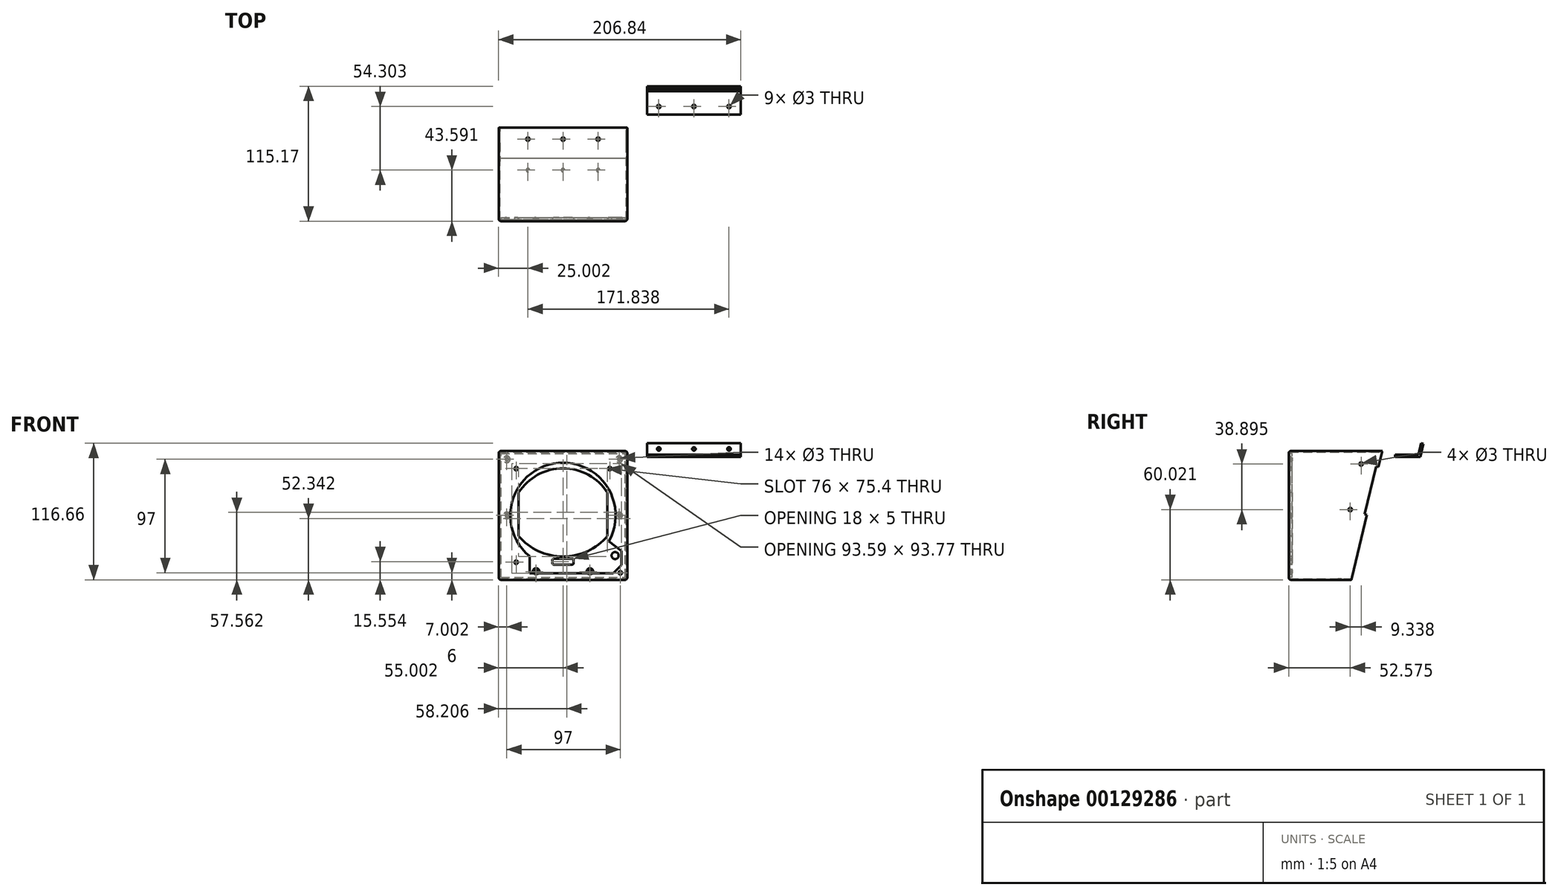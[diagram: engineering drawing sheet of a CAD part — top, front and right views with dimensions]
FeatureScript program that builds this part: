
annotation { "Feature Type Name" : "Feature", "Feature Type Description" : "" }
export const myFeature = defineFeature(function(context is Context, id is Id, definition is map)
    precondition{}
    {
        {
            var Q0;
            Q0=qCreatedBy(makeId("Front.planeOp"),FACE);
            var sketch = newSketch(context, id + "F0", { "sketchPlane" : qUnion([Q0])});
            skLineSegment(sketch, "E0.bottom", {"start": v(-56.84, -55) * mm, "end": v(-166.84, -55) * mm});
            skLineSegment(sketch, "E0.top", {"start": v(-56.84, 55) * mm, "end": v(-166.84, 55) * mm});
            skLineSegment(sketch, "E0.left", {"start": v(-56.84, -55) * mm, "end": v(-56.84, 55) * mm});
            skLineSegment(sketch, "E0.right", {"start": v(-166.84, -55) * mm, "end": v(-166.84, 55) * mm});
            skPoint(sketch, "E0.middle", {"position": v(-111.84, 0) * mm});
            skSolve(sketch);
        }
        {
            var Q0;
            Q0=makeQuery(id+"F0.imprint","IMPRINT",FACE,{"disambiguationData":[TD([[makeQuery(id+"F0.imprint","IMPRINT",EDGE,{"derivedFrom":sQuery(id+"F0.wireOp",EDGE,"E0.bottom")}),-1.0]])]});
            extrude(context, id + "F1", {"entities" : qUnion([Q0]), "endBound" : BoundingType.SYMMETRIC, "depth" : 120 * mm});
        }
        {
            var Q0;
            Q0=makeQuery(id+"F1.opExtrude","CAP_FACE",FACE,{"disambiguationData":[OSD([sQuery(id+"F0.wireOp",EDGE,"E0.bottom"),sQuery(id+"F0.wireOp",EDGE,"E0.top"),sQuery(id+"F0.wireOp",EDGE,"E0.left"),sQuery(id+"F0.wireOp",EDGE,"E0.right")])],"isStart":true});
            shell(context, id + "F2", {"entities" : qUnion([Q0]), "thickness" : 1 * mm});
        }
        {
            var Q0;
            Q0=makeQuery(id+"F1.opExtrude","SWEPT_FACE",FACE,{"disambiguationData":[OSD([sQuery(id+"F0.wireOp",EDGE,"E0.right")])]});
            var sketch = newSketch(context, id + "F3", { "sketchPlane" : qUnion([Q0])});
            skLineSegment(sketch, "E1", {"start": v(-20, 55) * mm, "end": v(6.4, -55) * mm});
            skLineSegment(sketch, "E2", {"start": v(6.4, -55) * mm, "end": v(-89.83, -55) * mm});
            skLineSegment(sketch, "E3", {"start": v(-89.83, -55) * mm, "end": v(-89.83, 55) * mm});
            skLineSegment(sketch, "E4", {"start": v(-89.83, 55) * mm, "end": v(-20, 55) * mm});
            skCircle(sketch, "E5", {"center": v(-1.91, 43.92) * mm, "radius": 1.5 * mm});
            skCircle(sketch, "E6", {"center": v(7.43, 5.02) * mm, "radius": 1.5 * mm});
            skLineSegment(sketch, "E7", {"start": v(-11.83, 20.97) * mm, "end": v(26.98, 30.28) * mm, "construction": true});
            skLineSegment(sketch, "E8", {"start": v(-16.73, 41.39) * mm, "end": v(-6.93, 0.55) * mm});
            skLineSegment(sketch, "E9", {"start": v(-6.93, 0.55) * mm, "end": v(-4.98, 1.01) * mm});
            skLineSegment(sketch, "E10", {"start": v(-4.98, 1.01) * mm, "end": v(-14.79, 41.85) * mm});
            skLineSegment(sketch, "E11", {"start": v(-14.79, 41.85) * mm, "end": v(-16.73, 41.39) * mm});
            skSolve(sketch);
        }
        {
            var Q0;
            Q0=qSketchRegion(id+"F3",true);
            extrude(context, id + "F4", {"entities" : qUnion([Q0]), "operationType" : NewBodyOperationType.REMOVE, "oppositeDirection" : true, "depth" : 110 * mm});
        }
        {
            var Q0;
            Q0=makeQuery(id+"F1.opExtrude","CAP_EDGE",EDGE,{"disambiguationData":[OSD([sQuery(id+"F0.wireOp",EDGE,"E0.right")])],"isStart":false});
            var Q1;
            Q1=makeQuery(id+"F1.opExtrude","SWEPT_EDGE",EDGE,{"disambiguationData":[OSD([sQuery(id+"F0.wireOp",EDGE,"E0.top"),sQuery(id+"F0.wireOp",EDGE,"E0.right")])]});
            var Q2;
            Q2=makeQuery(id+"F1.opExtrude","CAP_EDGE",EDGE,{"disambiguationData":[OSD([sQuery(id+"F0.wireOp",EDGE,"E0.top")])],"isStart":false});
            var Q3;
            Q3=makeQuery(id+"F1.opExtrude","CAP_EDGE",EDGE,{"disambiguationData":[OSD([sQuery(id+"F0.wireOp",EDGE,"E0.left")])],"isStart":false});
            var Q4;
            Q4=makeQuery(id+"F1.opExtrude","SWEPT_EDGE",EDGE,{"disambiguationData":[OSD([sQuery(id+"F0.wireOp",EDGE,"E0.top"),sQuery(id+"F0.wireOp",EDGE,"E0.left")])]});
            var Q5;
            Q5=makeQuery(id+"F1.opExtrude","CAP_EDGE",EDGE,{"disambiguationData":[OSD([sQuery(id+"F0.wireOp",EDGE,"E0.bottom")])],"isStart":false});
            var Q6;
            Q6=makeQuery(id+"F1.opExtrude","SWEPT_EDGE",EDGE,{"disambiguationData":[OSD([sQuery(id+"F0.wireOp",EDGE,"E0.bottom"),sQuery(id+"F0.wireOp",EDGE,"E0.left")])]});
            var Q7;
            Q7=makeQuery(id+"F1.opExtrude","SWEPT_EDGE",EDGE,{"disambiguationData":[OSD([sQuery(id+"F0.wireOp",EDGE,"E0.bottom"),sQuery(id+"F0.wireOp",EDGE,"E0.right")])]});
            fillet(context, id + "F5", {"entities" : qUnion([Q0, Q1, Q2, Q3, Q4, Q5, Q6, Q7]), "radius" : 2 * mm, "tangentPropagation" : true, "allowEdgeOverflow" : false});
        }
        {
            var Q0;
            Q0=makeQuery(id+"F1.opExtrude","CAP_FACE",FACE,{"disambiguationData":[OSD([sQuery(id+"F0.wireOp",EDGE,"E0.bottom"),sQuery(id+"F0.wireOp",EDGE,"E0.top"),sQuery(id+"F0.wireOp",EDGE,"E0.left"),sQuery(id+"F0.wireOp",EDGE,"E0.right")])],"isStart":false});
            var sketch = newSketch(context, id + "F6", { "sketchPlane" : qUnion([Q0])});
            skCircle(sketch, "E12", {"center": v(-111.84, 0) * mm, "radius": 45 * mm});
            skLineSegment(sketch, "E13", {"start": v(-140.4, -34.77) * mm, "end": v(-140.4, -49.54) * mm});
            skLineSegment(sketch, "E14", {"start": v(-140.4, -49.54) * mm, "end": v(-68.8, -49.54) * mm});
            skLineSegment(sketch, "E15", {"start": v(-68.8, -49.54) * mm, "end": v(-61.84, -42.48) * mm});
            skLineSegment(sketch, "E16", {"start": v(-61.84, -42.48) * mm, "end": v(-61.84, -30.48) * mm});
            skLineSegment(sketch, "E17", {"start": v(-61.84, -30.48) * mm, "end": v(-72.6, -22.03) * mm});
            skCircle(sketch, "E18", {"center": v(-151.84, 40) * mm, "radius": 1.5 * mm});
            skCircle(sketch, "E19", {"center": v(-71.84, 40) * mm, "radius": 1.5 * mm});
            skCircle(sketch, "E20", {"center": v(-151.84, -40) * mm, "radius": 1.5 * mm});
            skCircle(sketch, "E21", {"center": v(-62.84, -49) * mm, "radius": 1.5 * mm});
            skSolve(sketch);
        }
        {
            var Q0;
            Q0=qSketchRegion(id+"F6",true);
            extrude(context, id + "F7", {"entities" : qUnion([Q0]), "operationType" : NewBodyOperationType.REMOVE, "oppositeDirection" : true, "depth" : 1 * mm});
        }
        {
            var Q0;
            Q0=makeQuery(id+"F2.opShell","OFFSET_FACE",FACE,{"disambiguationData":[OSD([sQuery(id+"F0.wireOp",EDGE,"E0.bottom"),sQuery(id+"F0.wireOp",EDGE,"E0.top"),sQuery(id+"F0.wireOp",EDGE,"E0.left"),sQuery(id+"F0.wireOp",EDGE,"E0.right")])]});
            var sketch = newSketch(context, id + "F8", { "sketchPlane" : qUnion([Q0])});
            skLineSegment(sketch, "E22.bottom", {"start": v(164.84, -53) * mm, "end": v(58.84, -53) * mm});
            skLineSegment(sketch, "E22.top", {"start": v(164.84, 53) * mm, "end": v(58.84, 53) * mm});
            skLineSegment(sketch, "E22.left", {"start": v(164.84, -53) * mm, "end": v(164.84, 53) * mm});
            skLineSegment(sketch, "E22.right", {"start": v(58.84, -53) * mm, "end": v(58.84, 53) * mm});
            skPoint(sketch, "E22.middle", {"position": v(111.84, 0) * mm});
            skLineSegment(sketch, "E23", {"start": v(73.84, 19.37) * mm, "end": v(73.84, -17.63) * mm});
            skLineSegment(sketch, "E24", {"start": v(149.84, 19.37) * mm, "end": v(149.84, -17.63) * mm});
            skArc(sketch, "E25", {"start": v(149.84, 19.37) * mm, "mid": v(111.84, 40.26) * mm, "end": v(73.84, 19.37) * mm});
            skArc(sketch, "E26", {"start": v(73.84, -17.63) * mm, "mid": v(111.84, -35.14) * mm, "end": v(149.84, -17.63) * mm});
            skLineSegment(sketch, "E27.bottom", {"start": v(103.84, -36.95) * mm, "end": v(119.84, -36.95) * mm});
            skLineSegment(sketch, "E27.top", {"start": v(103.84, -41.95) * mm, "end": v(119.84, -41.95) * mm});
            skLineSegment(sketch, "E27.left", {"start": v(102.84, -37.95) * mm, "end": v(102.84, -40.95) * mm});
            skLineSegment(sketch, "E27.right", {"start": v(120.84, -37.95) * mm, "end": v(120.84, -40.95) * mm});
            skPoint(sketch, "E28.visualSharp", {"position": v(102.84, -36.95) * mm});
            skArc(sketch, "E28.filletArc", {"start": v(103.84, -36.95) * mm, "mid": v(103.13, -37.24) * mm, "end": v(102.84, -37.95) * mm});
            skPoint(sketch, "E29.visualSharp", {"position": v(102.84, -41.95) * mm});
            skArc(sketch, "E29.filletArc", {"start": v(102.84, -40.95) * mm, "mid": v(103.13, -41.65) * mm, "end": v(103.84, -41.95) * mm});
            skPoint(sketch, "E30.visualSharp", {"position": v(120.84, -36.95) * mm});
            skArc(sketch, "E30.filletArc", {"start": v(120.84, -37.95) * mm, "mid": v(120.55, -37.24) * mm, "end": v(119.84, -36.95) * mm});
            skPoint(sketch, "E31.visualSharp", {"position": v(120.84, -41.95) * mm});
            skArc(sketch, "E31.filletArc", {"start": v(119.84, -41.95) * mm, "mid": v(120.55, -41.65) * mm, "end": v(120.84, -40.95) * mm});
            skPoint(sketch, "E32", {"position": v(111.84, -39.45) * mm});
            skCircle(sketch, "E33", {"center": v(151.84, 40) * mm, "radius": 1.5 * mm});
            skCircle(sketch, "E34", {"center": v(71.84, 40) * mm, "radius": 1.5 * mm});
            skCircle(sketch, "E35", {"center": v(62.84, -49) * mm, "radius": 1.5 * mm});
            skCircle(sketch, "E36", {"center": v(151.84, -40) * mm, "radius": 1.5 * mm});
            skCircle(sketch, "E37", {"center": v(67.34, -34.27) * mm, "radius": 3 * mm});
            skSolve(sketch);
        }
        {
            var Q0;
            Q0=qSketchRegion(id+"F8",true);
            extrude(context, id + "F9", {"entities" : qUnion([Q0]), "depth" : 2 * mm});
        }
        {
            var Q0;
            Q0=makeQuery(id+"F9.opExtrude","CAP_FACE",FACE,{"disambiguationData":[OSD([sQuery(id+"F8.wireOp",EDGE,"E22.bottom"),sQuery(id+"F8.wireOp",EDGE,"E22.top"),sQuery(id+"F8.wireOp",EDGE,"E22.left"),sQuery(id+"F8.wireOp",EDGE,"E22.right"),sQuery(id+"F8.wireOp",EDGE,"E23"),sQuery(id+"F8.wireOp",EDGE,"E24"),sQuery(id+"F8.wireOp",EDGE,"E25"),sQuery(id+"F8.wireOp",EDGE,"E26"),sQuery(id+"F8.wireOp",EDGE,"E27.bottom"),sQuery(id+"F8.wireOp",EDGE,"E27.top"),sQuery(id+"F8.wireOp",EDGE,"E27.left"),sQuery(id+"F8.wireOp",EDGE,"E27.right"),sQuery(id+"F8.wireOp",EDGE,"E28.filletArc"),sQuery(id+"F8.wireOp",EDGE,"E29.filletArc"),sQuery(id+"F8.wireOp",EDGE,"E30.filletArc"),sQuery(id+"F8.wireOp",EDGE,"E31.filletArc"),sQuery(id+"F8.wireOp",EDGE,"E33"),sQuery(id+"F8.wireOp",EDGE,"E34"),sQuery(id+"F8.wireOp",EDGE,"E35"),sQuery(id+"F8.wireOp",EDGE,"E36"),sQuery(id+"F8.wireOp",EDGE,"E37")])],"isStart":true});
            var sketch = newSketch(context, id + "F10", { "sketchPlane" : qUnion([Q0])});
            skLineSegment(sketch, "E38.bottom", {"start": v(-72.84, -43) * mm, "end": v(-150.84, -43) * mm});
            skLineSegment(sketch, "E38.top", {"start": v(-72.84, 43) * mm, "end": v(-150.84, 43) * mm});
            skLineSegment(sketch, "E38.left", {"start": v(-72.84, -43) * mm, "end": v(-72.84, 43) * mm});
            skLineSegment(sketch, "E38.right", {"start": v(-150.84, -43) * mm, "end": v(-150.84, 43) * mm});
            skPoint(sketch, "E38.middle", {"position": v(-111.84, 0) * mm});
            skLineSegment(sketch, "E39.bottom", {"start": v(-56.84, -55) * mm, "end": v(-166.84, -55) * mm});
            skLineSegment(sketch, "E39.top", {"start": v(-56.84, 55) * mm, "end": v(-166.84, 55) * mm});
            skLineSegment(sketch, "E39.left", {"start": v(-56.84, -55) * mm, "end": v(-56.84, 55) * mm});
            skLineSegment(sketch, "E39.right", {"start": v(-166.84, -55) * mm, "end": v(-166.84, 55) * mm});
            skSolve(sketch);
        }
        {
            var Q0;
            {var subQ10=sQuery(id+"F10.wireOp",EDGE,"E38.bottom");Q0=makeQuery(id+"F10.imprint","IMPRINT",FACE,{"disambiguationData":[TD([[makeQuery(id+"F10.imprint","IMPRINT",EDGE,{"derivedFrom":subQ10}),1.0]])]});}
            var sketch = newSketch(context, id + "F11", { "sketchPlane" : qUnion([Q0])});
            skCircle(sketch, "E40", {"center": v(-159.84, 48) * mm, "radius": 1.5 * mm});
            skCircle(sketch, "E41", {"center": v(-63.84, 48) * mm, "radius": 1.5 * mm});
            skCircle(sketch, "E42", {"center": v(-88.84, -48) * mm, "radius": 1.5 * mm});
            skCircle(sketch, "E43", {"center": v(-134.84, -48) * mm, "radius": 1.5 * mm});
            skCircle(sketch, "E44", {"center": v(-159.84, 0) * mm, "radius": 1.5 * mm});
            skCircle(sketch, "E45", {"center": v(-63.84, 0) * mm, "radius": 1.5 * mm});
            skSolve(sketch);
        }
        {
            var Q0;
            Q0=sQuery(id+"F11.wireOp",VERTEX,"E43.center");
            var Q1;
            Q1=sQuery(id+"F11.wireOp",VERTEX,"E42.center");
            var Q2;
            Q2=sQuery(id+"F11.wireOp",VERTEX,"E40.center");
            var Q3;
            Q3=sQuery(id+"F11.wireOp",VERTEX,"E41.center");
            var Q4;
            Q4=sQuery(id+"F11.wireOp",VERTEX,"E44.center");
            var Q5;
            Q5=sQuery(id+"F11.wireOp",VERTEX,"E45.center");
            var Q6;
            Q6=makeQuery(id+"F9.opExtrude","SWEPT_BODY",BODY,{"disambiguationData":[OSD([sQuery(id+"F8.wireOp",EDGE,"E22.bottom"),sQuery(id+"F8.wireOp",EDGE,"E22.top"),sQuery(id+"F8.wireOp",EDGE,"E22.left"),sQuery(id+"F8.wireOp",EDGE,"E22.right"),sQuery(id+"F8.wireOp",EDGE,"E23"),sQuery(id+"F8.wireOp",EDGE,"E24"),sQuery(id+"F8.wireOp",EDGE,"E25"),sQuery(id+"F8.wireOp",EDGE,"E26"),sQuery(id+"F8.wireOp",EDGE,"E27.bottom"),sQuery(id+"F8.wireOp",EDGE,"E27.top"),sQuery(id+"F8.wireOp",EDGE,"E27.left"),sQuery(id+"F8.wireOp",EDGE,"E27.right"),sQuery(id+"F8.wireOp",EDGE,"E28.filletArc"),sQuery(id+"F8.wireOp",EDGE,"E29.filletArc"),sQuery(id+"F8.wireOp",EDGE,"E30.filletArc"),sQuery(id+"F8.wireOp",EDGE,"E31.filletArc"),sQuery(id+"F8.wireOp",EDGE,"E33"),sQuery(id+"F8.wireOp",EDGE,"E34"),sQuery(id+"F8.wireOp",EDGE,"E35"),sQuery(id+"F8.wireOp",EDGE,"E36"),sQuery(id+"F8.wireOp",EDGE,"E37")])]});
            hole(context, id + "F12", {"style" : HoleStyle.C_SINK, "endStyle" : HoleEndStyle.THROUGH, "holeDiameter" : 3 * mm, "cSinkDiameter" : 5.7 * mm, "cSinkAngle" : 90 * degree, "locations" : qUnion([Q0, Q1, Q2, Q3, Q4, Q5]), "scope" : qUnion([Q6]), "isTappedThrough" : true});
        }
        {
            var Q0;
            Q0=makeQuery(id+"F1.opExtrude","SWEPT_FACE",FACE,{"disambiguationData":[OSD([sQuery(id+"F0.wireOp",EDGE,"E0.top")])]});
            var sketch = newSketch(context, id + "F13", { "sketchPlane" : qUnion([Q0])});
            skCircle(sketch, "E46", {"center": v(-141.84, 10) * mm, "radius": 1.5 * mm});
            skCircle(sketch, "E47", {"center": v(-81.84, 10) * mm, "radius": 1.5 * mm});
            skCircle(sketch, "E48", {"center": v(-111.84, 10) * mm, "radius": 1.5 * mm});
            skSolve(sketch);
        }
        {
            var Q0;
            Q0=makeQuery(id+"F1.opExtrude","SWEPT_FACE",FACE,{"disambiguationData":[OSD([sQuery(id+"F0.wireOp",EDGE,"E0.bottom")])]});
            var sketch = newSketch(context, id + "F14", { "sketchPlane" : qUnion([Q0])});
            skCircle(sketch, "E49", {"center": v(-141.84, 16.4) * mm, "radius": 1.5 * mm});
            skCircle(sketch, "E50", {"center": v(-81.84, 16.4) * mm, "radius": 1.5 * mm});
            skCircle(sketch, "E51", {"center": v(-111.84, 16.4) * mm, "radius": 1.5 * mm});
            skSolve(sketch);
        }
        {
            var Q0;
            Q0=qSketchRegion(id+"F13",true);
            var Q1;
            Q1=qSketchRegion(id+"F14",true);
            extrude(context, id + "F15", {"entities" : qUnion([Q0, Q1]), "operationType" : NewBodyOperationType.REMOVE, "oppositeDirection" : true, "depth" : 2 * mm});
        }
        {
            var Q0;
            Q0=qSketchRegion(id+"F14",true);
            extrude(context, id + "F16", {"entities" : qUnion([Q0]), "operationType" : NewBodyOperationType.REMOVE, "oppositeDirection" : true, "depth" : 2 * mm});
        }
        {
            var Q0;
            Q0=qCreatedBy(makeId("Right.planeOp"),FACE);
            var sketch = newSketch(context, id + "F17", { "sketchPlane" : qUnion([Q0])});
            skLineSegment(sketch, "E52", {"start": v(55.17, 61.2) * mm, "end": v(52.47, 49.94) * mm});
            skLineSegment(sketch, "E53", {"start": v(52.47, 49.94) * mm, "end": v(30.9, 49.94) * mm});
            skLineSegment(sketch, "E54", {"start": v(30.9, 49.94) * mm, "end": v(30.9, 51.94) * mm});
            skLineSegment(sketch, "E55", {"start": v(30.9, 51.94) * mm, "end": v(50.9, 51.94) * mm});
            skLineSegment(sketch, "E56", {"start": v(50.9, 51.94) * mm, "end": v(53.23, 61.66) * mm});
            skLineSegment(sketch, "E57", {"start": v(53.23, 61.66) * mm, "end": v(55.17, 61.2) * mm});
            skSolve(sketch);
        }
        {
            var Q0;
            Q0=qSketchRegion(id+"F17",true);
            extrude(context, id + "F18", {"entities" : qUnion([Q0]), "endBound" : BoundingType.SYMMETRIC, "depth" : 80 * mm});
        }
        {
            var Q0;
            Q0=makeQuery(id+"F18.opExtrude","SWEPT_FACE",FACE,{"disambiguationData":[OSD([sQuery(id+"F17.wireOp",EDGE,"E55")])]});
            var sketch = newSketch(context, id + "F19", { "sketchPlane" : qUnion([Q0])});
            skCircle(sketch, "E58", {"center": v(-30, 37.9) * mm, "radius": 1.5 * mm});
            skCircle(sketch, "E59", {"center": v(0, 37.9) * mm, "radius": 1.5 * mm});
            skCircle(sketch, "E60", {"center": v(30, 37.9) * mm, "radius": 1.5 * mm});
            skSolve(sketch);
        }
        {
            var Q0;
            Q0=makeQuery(id+"F18.opExtrude","SWEPT_FACE",FACE,{"disambiguationData":[OSD([sQuery(id+"F17.wireOp",EDGE,"E56")])]});
            var sketch = newSketch(context, id + "F20", { "sketchPlane" : qUnion([Q0])});
            skCircle(sketch, "E61", {"center": v(-30, 67.38) * mm, "radius": 1.5 * mm});
            skCircle(sketch, "E62", {"center": v(0, 67.38) * mm, "radius": 1.5 * mm});
            skCircle(sketch, "E63", {"center": v(30, 67.38) * mm, "radius": 1.5 * mm});
            skSolve(sketch);
        }
        {
            var Q0;
            Q0=sQuery(id+"F20.wireOp",VERTEX,"E61.center");
            var Q1;
            Q1=sQuery(id+"F19.wireOp",VERTEX,"E58.center");
            var Q2;
            Q2=sQuery(id+"F20.wireOp",VERTEX,"E62.center");
            var Q3;
            Q3=sQuery(id+"F19.wireOp",VERTEX,"E59.center");
            var Q4;
            Q4=sQuery(id+"F20.wireOp",VERTEX,"E63.center");
            var Q5;
            Q5=sQuery(id+"F19.wireOp",VERTEX,"E60.center");
            var Q6;
            Q6=makeQuery(id+"F18.opExtrude","SWEPT_BODY",BODY,{"disambiguationData":[OSD([sQuery(id+"F17.wireOp",EDGE,"E52"),sQuery(id+"F17.wireOp",EDGE,"E53"),sQuery(id+"F17.wireOp",EDGE,"E54"),sQuery(id+"F17.wireOp",EDGE,"E55"),sQuery(id+"F17.wireOp",EDGE,"E56"),sQuery(id+"F17.wireOp",EDGE,"E57")])]});
            hole(context, id + "F21", {"style" : HoleStyle.SIMPLE, "endStyle" : HoleEndStyle.THROUGH, "holeDiameter" : 3 * mm, "locations" : qUnion([Q0, Q1, Q2, Q3, Q4, Q5]), "scope" : qUnion([Q6]), "isTappedThrough" : true});
        }
    });
